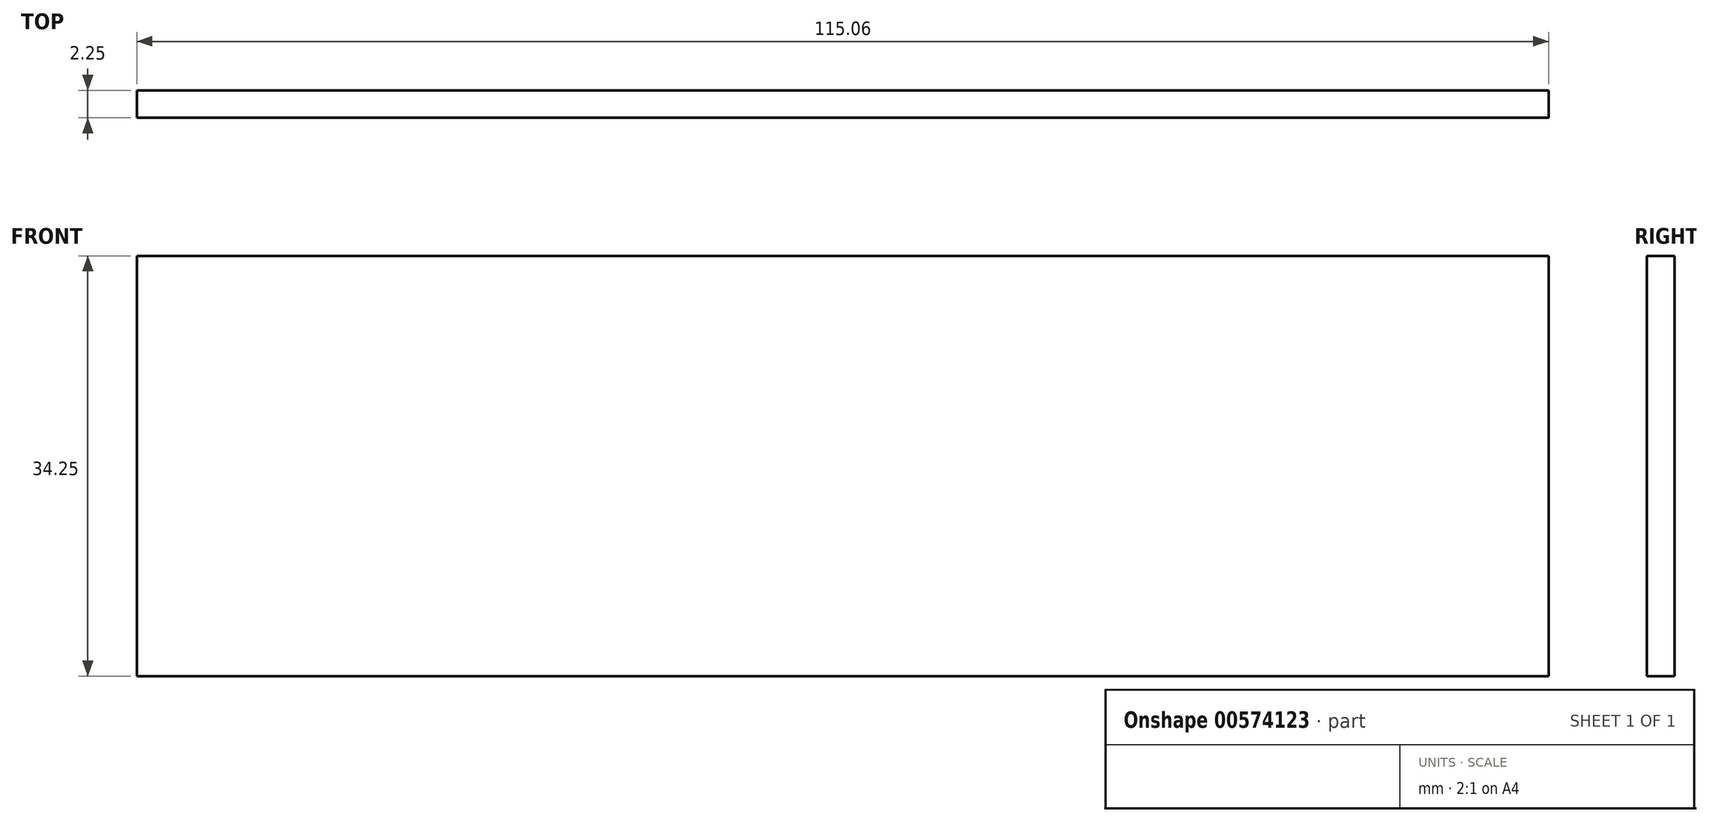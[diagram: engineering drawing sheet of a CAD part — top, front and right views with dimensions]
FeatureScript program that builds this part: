
annotation { "Feature Type Name" : "Feature", "Feature Type Description" : "" }
export const myFeature = defineFeature(function(context is Context, id is Id, definition is map)
    precondition{}
    {
        {
            var Q0;
            Q0=qCreatedBy(makeId("Front.planeOp"),FACE);
            var sketch = newSketch(context, id + "F0", { "sketchPlane" : qUnion([Q0])});
            skLineSegment(sketch, "E0.bottom", {"start": v(0, 0) * mm, "end": v(115.06, 0) * mm});
            skLineSegment(sketch, "E0.top", {"start": v(0, -34.25) * mm, "end": v(115.06, -34.25) * mm});
            skLineSegment(sketch, "E0.left", {"start": v(0, 0) * mm, "end": v(0, -34.25) * mm});
            skLineSegment(sketch, "E0.right", {"start": v(115.06, 0) * mm, "end": v(115.06, -34.25) * mm});
            skSolve(sketch);
        }
        {
            var Q0;
            Q0=makeQuery(id+"F0.imprint","IMPRINT",FACE,{"disambiguationData":[TD([[makeQuery(id+"F0.imprint","IMPRINT",EDGE,{"derivedFrom":sQuery(id+"F0.wireOp",EDGE,"E0.bottom")}),-1.0]])]});
            extrude(context, id + "F1", {"entities" : qUnion([Q0]), "depth" : 2.25 * mm, "offsetDistance" : 25.4 * mm});
        }
    });
